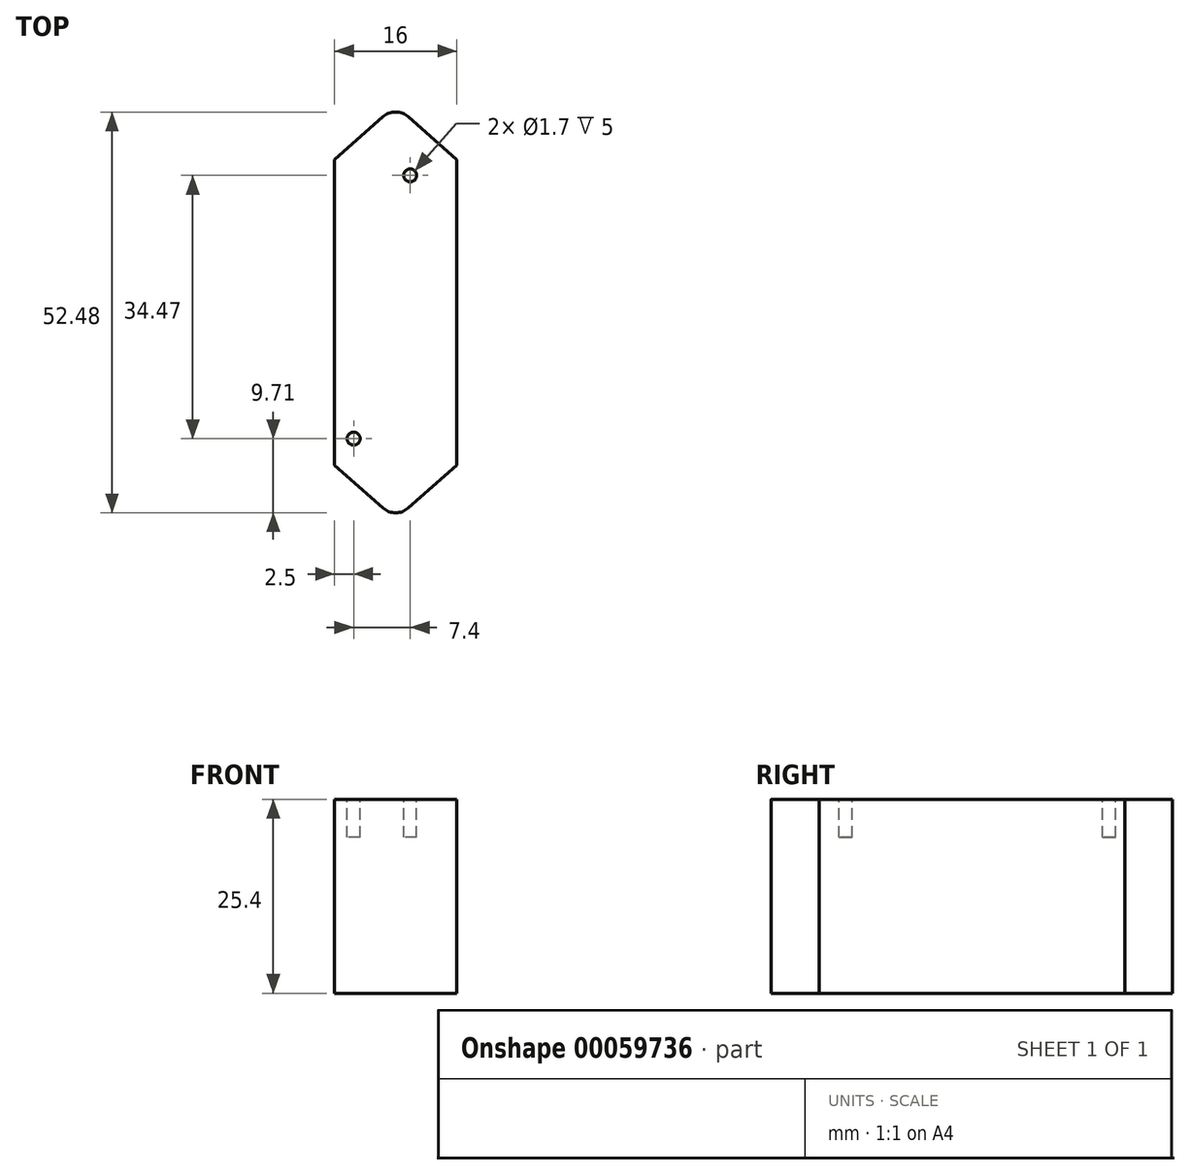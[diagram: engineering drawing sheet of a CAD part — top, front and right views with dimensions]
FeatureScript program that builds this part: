
annotation { "Feature Type Name" : "Feature", "Feature Type Description" : "" }
export const myFeature = defineFeature(function(context is Context, id is Id, definition is map)
    precondition{}
    {
        {
            var Q0;
            Q0=qCreatedBy(makeId("Top.planeOp"),FACE);
            var sketch = newSketch(context, id + "F0", { "sketchPlane" : qUnion([Q0])});
            skCircle(sketch, "E0", {"center": v(1.9, 17.94) * mm, "radius": 0.85 * mm});
            skCircle(sketch, "E1", {"center": v(-5.5, -16.53) * mm, "radius": 0.85 * mm});
            skCircle(sketch, "E2.0", {"center": v(0, -23.74) * mm, "radius": 1.32 * mm});
            skCircle(sketch, "E3.0", {"center": v(0, 23.74) * mm, "radius": 1.32 * mm});
            skCircle(sketch, "E4", {"center": v(1.27, -15.74) * mm, "radius": 0.45 * mm, "construction": true});
            skCircle(sketch, "E5.0.1.0", {"center": v(1.27, -13.2) * mm, "radius": 0.45 * mm, "construction": true});
            skCircle(sketch, "E5.0.2.0", {"center": v(1.27, -10.66) * mm, "radius": 0.45 * mm, "construction": true});
            skCircle(sketch, "E5.0.3.0", {"center": v(1.27, -8.12) * mm, "radius": 0.45 * mm, "construction": true});
            skCircle(sketch, "E5.0.4.0", {"center": v(1.27, -5.58) * mm, "radius": 0.45 * mm, "construction": true});
            skCircle(sketch, "E5.0.5.0", {"center": v(1.27, -3.04) * mm, "radius": 0.45 * mm, "construction": true});
            skCircle(sketch, "E5.0.6.0", {"center": v(1.27, -0.5) * mm, "radius": 0.45 * mm, "construction": true});
            skCircle(sketch, "E5.0.7.0", {"center": v(1.27, 2.04) * mm, "radius": 0.45 * mm, "construction": true});
            skCircle(sketch, "E5.0.8.0", {"center": v(1.27, 4.58) * mm, "radius": 0.45 * mm, "construction": true});
            skCircle(sketch, "E5.0.9.0", {"center": v(1.27, 7.12) * mm, "radius": 0.45 * mm, "construction": true});
            skCircle(sketch, "E5.0.10.0", {"center": v(1.27, 9.66) * mm, "radius": 0.45 * mm, "construction": true});
            skCircle(sketch, "E5.0.11.0", {"center": v(1.27, 12.2) * mm, "radius": 0.45 * mm, "construction": true});
            skCircle(sketch, "E5.0.12.0", {"center": v(1.27, 14.74) * mm, "radius": 0.45 * mm, "construction": true});
            skLineSegment(sketch, "E5.direction1", {"start": v(1.27, -15.74) * mm, "end": v(-1.27, -15.74) * mm, "construction": true});
            skLineSegment(sketch, "E5.direction2", {"start": v(1.27, -15.74) * mm, "end": v(1.27, -13.2) * mm, "construction": true});
            skCircle(sketch, "E6.0.1.0", {"center": v(-1.27, -15.74) * mm, "radius": 0.45 * mm, "construction": true});
            skCircle(sketch, "E6.0.1.1", {"center": v(-1.27, -13.2) * mm, "radius": 0.45 * mm, "construction": true});
            skCircle(sketch, "E6.0.1.2", {"center": v(-1.27, -10.66) * mm, "radius": 0.45 * mm, "construction": true});
            skCircle(sketch, "E6.0.1.3", {"center": v(-1.27, -8.12) * mm, "radius": 0.45 * mm, "construction": true});
            skCircle(sketch, "E6.0.1.4", {"center": v(-1.27, -5.58) * mm, "radius": 0.45 * mm, "construction": true});
            skCircle(sketch, "E6.0.1.5", {"center": v(-1.27, -3.04) * mm, "radius": 0.45 * mm, "construction": true});
            skCircle(sketch, "E6.0.1.6", {"center": v(-1.27, -0.5) * mm, "radius": 0.45 * mm, "construction": true});
            skCircle(sketch, "E6.0.1.7", {"center": v(-1.27, 2.04) * mm, "radius": 0.45 * mm, "construction": true});
            skCircle(sketch, "E6.0.1.8", {"center": v(-1.27, 4.58) * mm, "radius": 0.45 * mm, "construction": true});
            skCircle(sketch, "E6.0.1.9", {"center": v(-1.27, 7.12) * mm, "radius": 0.45 * mm, "construction": true});
            skCircle(sketch, "E6.0.1.10", {"center": v(-1.27, 9.66) * mm, "radius": 0.45 * mm, "construction": true});
            skCircle(sketch, "E6.0.1.11", {"center": v(-1.27, 12.2) * mm, "radius": 0.45 * mm, "construction": true});
            skCircle(sketch, "E6.0.1.12", {"center": v(-1.27, 14.74) * mm, "radius": 0.45 * mm, "construction": true});
            skLineSegment(sketch, "E7", {"start": v(0, 23.74) * mm, "end": v(0, -23.74) * mm, "construction": true});
            skCircle(sketch, "E8", {"center": v(0, 23.74) * mm, "radius": 2.5 * mm});
            skCircle(sketch, "E9.MirrorC", {"center": v(0, -23.74) * mm, "radius": 2.5 * mm});
            skLineSegment(sketch, "E10.bottom", {"start": v(8, 20) * mm, "end": v(-8, 20) * mm});
            skLineSegment(sketch, "E10.top", {"start": v(8, -20) * mm, "end": v(-8, -20) * mm});
            skLineSegment(sketch, "E10.left", {"start": v(8, 20) * mm, "end": v(8, -20) * mm});
            skLineSegment(sketch, "E10.right", {"start": v(-8, 20) * mm, "end": v(-8, -20) * mm});
            skPoint(sketch, "E10.middle", {"position": v(0, 0) * mm});
            skLineSegment(sketch, "E11", {"start": v(-1.66, 25.61) * mm, "end": v(-8, 20) * mm});
            skLineSegment(sketch, "E12.MirrorCS", {"start": v(1.66, 25.61) * mm, "end": v(8, 20) * mm});
            skLineSegment(sketch, "E13.MirrorCS", {"start": v(1.66, -25.61) * mm, "end": v(8, -20) * mm});
            skLineSegment(sketch, "E14.MirrorCS", {"start": v(-1.66, -25.61) * mm, "end": v(-8, -20) * mm});
            skLineSegment(sketch, "E15.bottom", {"start": v(-1.72, 15.2) * mm, "end": v(1.72, 15.2) * mm, "construction": true});
            skLineSegment(sketch, "E15.top", {"start": v(-1.72, -16.2) * mm, "end": v(1.72, -16.2) * mm, "construction": true});
            skLineSegment(sketch, "E15.left", {"start": v(-1.72, 15.2) * mm, "end": v(-1.72, -16.2) * mm, "construction": true});
            skLineSegment(sketch, "E15.right", {"start": v(1.72, 15.2) * mm, "end": v(1.72, -16.2) * mm, "construction": true});
            skLineSegment(sketch, "E16.0", {"start": v(3.22, 16.7) * mm, "end": v(3.22, -17.7) * mm, "construction": true});
            skLineSegment(sketch, "E16.1", {"start": v(-3.22, 16.7) * mm, "end": v(3.22, 16.7) * mm, "construction": true});
            skLineSegment(sketch, "E16.2", {"start": v(-3.22, 16.7) * mm, "end": v(-3.22, -17.7) * mm, "construction": true});
            skLineSegment(sketch, "E16.3", {"start": v(-3.22, -17.7) * mm, "end": v(3.22, -17.7) * mm, "construction": true});
            skLineSegment(sketch, "E17", {"start": v(1.72, -0.5) * mm, "end": v(-1.72, -0.5) * mm, "construction": true});
            skSolve(sketch);
        }
        {
            var Q0;
            Q0=makeQuery(id+"F0.imprint","IMPRINT",FACE,{"disambiguationData":[TD([[makeQuery(id+"F0.imprint","IMPRINT",EDGE,{"derivedFrom":sQuery(id+"F0.wireOp",EDGE,"E3.0")}),-1.0]])]});
            var Q1;
            Q1=makeQuery(id+"F0.imprint","IMPRINT",FACE,{"disambiguationData":[TD([[makeQuery(id+"F0.imprint","IMPRINT",EDGE,{"derivedFrom":sQuery(id+"F0.wireOp",EDGE,"E2.0")}),-1.0]])]});
            var Q2;
            Q2=makeQuery(id+"F0.imprint","IMPRINT",FACE,{"disambiguationData":[TD([[makeQuery(id+"F0.imprint","IMPRINT",EDGE,{"derivedFrom":sQuery(id+"F0.wireOp",EDGE,"E10.top")}),1.0]])]});
            var Q3;
            Q3=makeQuery(id+"F0.imprint","IMPRINT",FACE,{"disambiguationData":[TD([[makeQuery(id+"F0.imprint","IMPRINT",EDGE,{"derivedFrom":sQuery(id+"F0.wireOp",EDGE,"E0")}),-1.0]])]});
            var Q4;
            Q4=makeQuery(id+"F0.imprint","IMPRINT",FACE,{"disambiguationData":[TD([[makeQuery(id+"F0.imprint","IMPRINT",EDGE,{"derivedFrom":sQuery(id+"F0.wireOp",EDGE,"E1")}),1.0]])]});
            var Q5;
            Q5=makeQuery(id+"F0.imprint","IMPRINT",FACE,{"disambiguationData":[TD([[makeQuery(id+"F0.imprint","IMPRINT",EDGE,{"derivedFrom":sQuery(id+"F0.wireOp",EDGE,"E0")}),1.0]])]});
            var Q6;
            Q6=makeQuery(id+"F0.imprint","IMPRINT",FACE,{"disambiguationData":[TD([[makeQuery(id+"F0.imprint","IMPRINT",EDGE,{"derivedFrom":sQuery(id+"F0.wireOp",EDGE,"E10.bottom")}),-1.0]])]});
            var Q7;
            Q7=makeQuery(id+"F0.imprint","IMPRINT",FACE,{"disambiguationData":[TD([[makeQuery(id+"F0.imprint","IMPRINT",EDGE,{"derivedFrom":sQuery(id+"F0.wireOp",EDGE,"E2.0")}),1.0]])]});
            var Q8;
            Q8=makeQuery(id+"F0.imprint","IMPRINT",FACE,{"disambiguationData":[TD([[makeQuery(id+"F0.imprint","IMPRINT",EDGE,{"derivedFrom":sQuery(id+"F0.wireOp",EDGE,"E3.0")}),1.0]])]});
            extrude(context, id + "F1", {"entities" : qUnion([Q0, Q1, Q2, Q3, Q4, Q5, Q6, Q7, Q8]), "depth" : 25.4 * mm});
        }
        {
            var Q0;
            Q0=makeQuery(id+"F1.opExtrude","CAP_FACE",FACE,{"disambiguationData":[OSD([sQuery(id+"F0.wireOp",EDGE,"E2.0"),sQuery(id+"F0.wireOp",EDGE,"E3.0"),sQuery(id+"F0.wireOp",EDGE,"E8"),sQuery(id+"F0.wireOp",EDGE,"E9.MirrorC"),sQuery(id+"F0.wireOp",EDGE,"E10.left"),sQuery(id+"F0.wireOp",EDGE,"E10.right"),sQuery(id+"F0.wireOp",EDGE,"E11"),sQuery(id+"F0.wireOp",EDGE,"E12.MirrorCS"),sQuery(id+"F0.wireOp",EDGE,"E13.MirrorCS"),sQuery(id+"F0.wireOp",EDGE,"E14.MirrorCS")])],"isStart":false});
            var sketch = newSketch(context, id + "F2", { "sketchPlane" : qUnion([Q0])});
            skCircle(sketch, "E18.0", {"center": v(1.9, 17.94) * mm, "radius": 0.85 * mm});
            skCircle(sketch, "E18.1", {"center": v(-5.5, -16.53) * mm, "radius": 0.85 * mm});
            skSolve(sketch);
        }
        {
            var Q0;
            Q0 = qSketchRegion(id + "F2", true);
            extrude(context, id + "F3", {"entities" : qUnion([Q0]), "operationType" : NewBodyOperationType.REMOVE, "oppositeDirection" : true, "depth" : 5 * mm});
        }
    });
